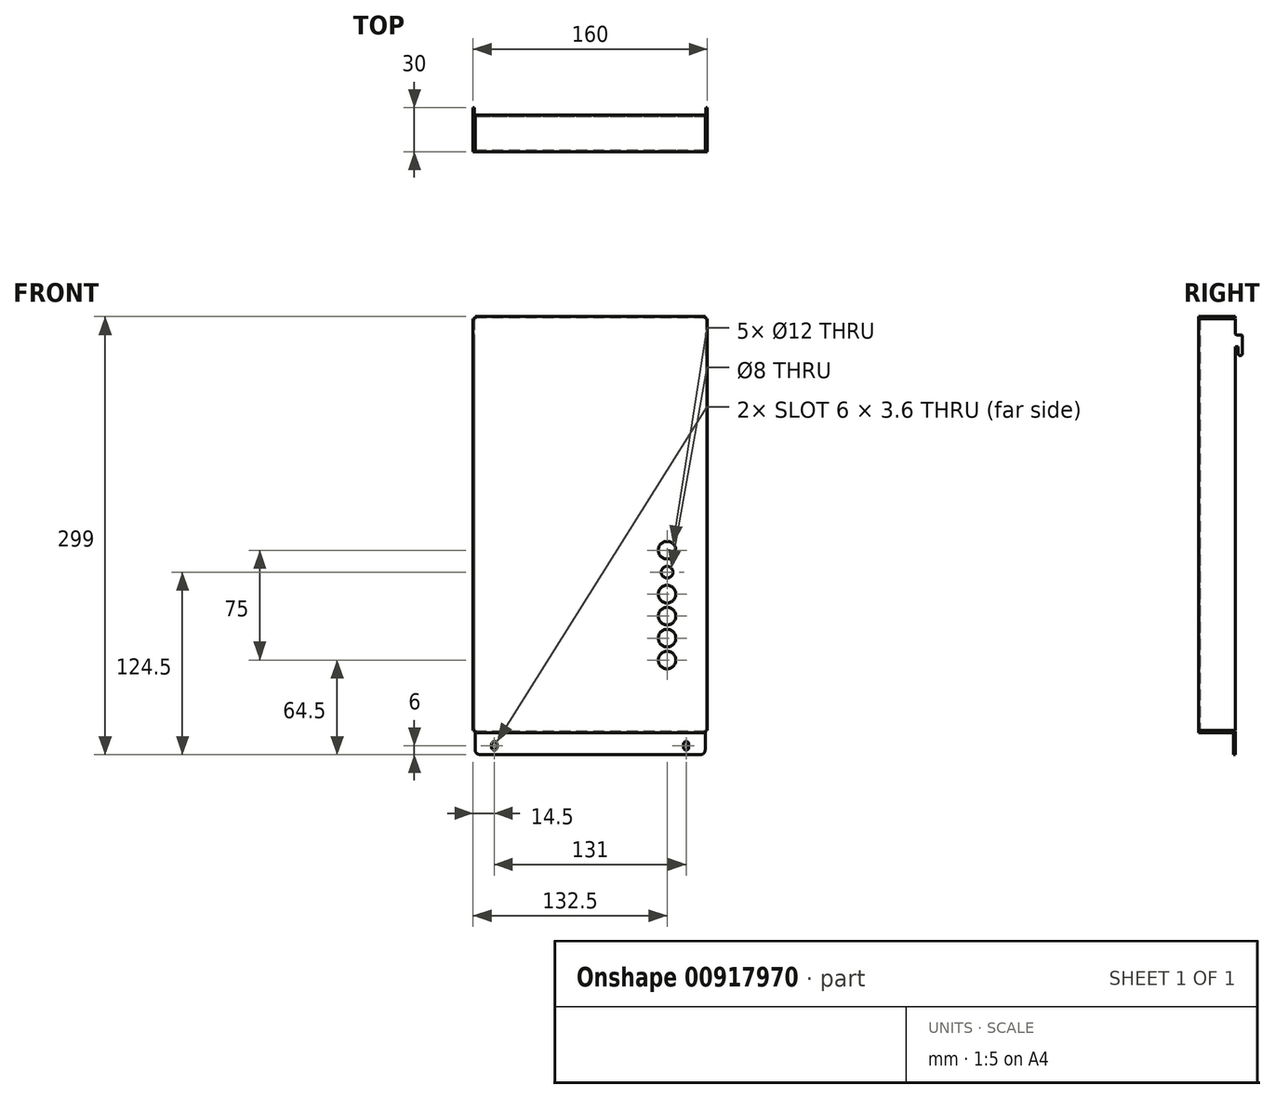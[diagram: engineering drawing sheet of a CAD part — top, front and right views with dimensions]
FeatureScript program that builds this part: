
annotation { "Feature Type Name" : "Feature", "Feature Type Description" : "" }
export const myFeature = defineFeature(function(context is Context, id is Id, definition is map)
    precondition{}
    {
        {
            var Q0;
            Q0=qCreatedBy(makeId("Front.planeOp"),FACE);
            var sketch = newSketch(context, id + "F0", { "sketchPlane" : qUnion([Q0])});
            skLineSegment(sketch, "E0.bottom", {"start": v(0, 0) * mm, "end": v(160, 0) * mm});
            skLineSegment(sketch, "E0.top", {"start": v(0, 284) * mm, "end": v(160, 284) * mm});
            skLineSegment(sketch, "E0.left", {"start": v(0, 0) * mm, "end": v(0, 284) * mm});
            skLineSegment(sketch, "E0.right", {"start": v(160, 0) * mm, "end": v(160, 284) * mm});
            skSolve(sketch);
        }
        {
            var Q0;
            Q0 = qSketchRegion(id + "F0", true);
            extrude(context, id + "F1", {"entities" : qUnion([Q0]), "depth" : 1 * mm, "offsetDistance" : 25 * mm});
        }
        {
            var Q0;
            Q0=makeQuery(id+"F1.opExtrude","CAP_FACE",FACE,{"disambiguationData":[OSD([sQuery(id+"F0.wireOp",EDGE,"E0.bottom"),sQuery(id+"F0.wireOp",EDGE,"E0.top"),sQuery(id+"F0.wireOp",EDGE,"E0.left"),sQuery(id+"F0.wireOp",EDGE,"E0.right")])],"isStart":true});
            var sketch = newSketch(context, id + "F2", { "sketchPlane" : qUnion([Q0])});
            skLineSegment(sketch, "E1.bottom", {"start": v(-160, 284) * mm, "end": v(0, 284) * mm});
            skLineSegment(sketch, "E1.top", {"start": v(-160, 0) * mm, "end": v(0, 0) * mm});
            skLineSegment(sketch, "E1.left", {"start": v(-160, 284) * mm, "end": v(-160, 0) * mm});
            skLineSegment(sketch, "E1.right", {"start": v(0, 284) * mm, "end": v(0, 0) * mm});
            skLineSegment(sketch, "E2.0", {"start": v(-1, 283) * mm, "end": v(-1, 1) * mm});
            skLineSegment(sketch, "E3.0", {"start": v(-159, 283) * mm, "end": v(-159, 1) * mm});
            skLineSegment(sketch, "E4.0", {"start": v(-159, 283) * mm, "end": v(-1, 283) * mm});
            skLineSegment(sketch, "E5.0", {"start": v(-159, 1) * mm, "end": v(-1, 1) * mm});
            skSolve(sketch);
        }
        {
            var Q0;
            Q0 = qSketchRegion(id + "F2", true);
            extrude(context, id + "F3", {"entities" : qUnion([Q0]), "operationType" : NewBodyOperationType.ADD, "depth" : 24 * mm, "offsetDistance" : 25 * mm});
        }
        {
            var Q0;
            Q0=makeQuery(id+"F1.opExtrude","CAP_FACE",FACE,{"disambiguationData":[OSD([sQuery(id+"F0.wireOp",EDGE,"E0.bottom"),sQuery(id+"F0.wireOp",EDGE,"E0.top"),sQuery(id+"F0.wireOp",EDGE,"E0.left"),sQuery(id+"F0.wireOp",EDGE,"E0.right")])],"isStart":false});
            var sketch = newSketch(context, id + "F4", { "sketchPlane" : qUnion([Q0])});
            skLineSegment(sketch, "E6.bottom", {"start": v(0, 284) * mm, "end": v(1.5, 284) * mm});
            skLineSegment(sketch, "E6.top", {"start": v(0, 282.5) * mm, "end": v(1.5, 282.5) * mm});
            skLineSegment(sketch, "E6.left", {"start": v(0, 284) * mm, "end": v(0, 282.5) * mm});
            skLineSegment(sketch, "E6.right", {"start": v(1.5, 284) * mm, "end": v(1.5, 282.5) * mm});
            skLineSegment(sketch, "E7.bottom", {"start": v(160, 284) * mm, "end": v(158.5, 284) * mm});
            skLineSegment(sketch, "E7.top", {"start": v(160, 282.5) * mm, "end": v(158.5, 282.5) * mm});
            skLineSegment(sketch, "E7.left", {"start": v(160, 284) * mm, "end": v(160, 282.5) * mm});
            skLineSegment(sketch, "E7.right", {"start": v(158.5, 284) * mm, "end": v(158.5, 282.5) * mm});
            skLineSegment(sketch, "E8.bottom", {"start": v(160, 0) * mm, "end": v(158.5, 0) * mm});
            skLineSegment(sketch, "E8.top", {"start": v(160, 1.5) * mm, "end": v(158.5, 1.5) * mm});
            skLineSegment(sketch, "E8.left", {"start": v(160, 0) * mm, "end": v(160, 1.5) * mm});
            skLineSegment(sketch, "E8.right", {"start": v(158.5, 0) * mm, "end": v(158.5, 1.5) * mm});
            skLineSegment(sketch, "E9.bottom", {"start": v(0, 0) * mm, "end": v(1.5, 0) * mm});
            skLineSegment(sketch, "E9.top", {"start": v(0, 1.5) * mm, "end": v(1.5, 1.5) * mm});
            skLineSegment(sketch, "E9.left", {"start": v(0, 0) * mm, "end": v(0, 1.5) * mm});
            skLineSegment(sketch, "E9.right", {"start": v(1.5, 0) * mm, "end": v(1.5, 1.5) * mm});
            skSolve(sketch);
        }
        {
            var Q0;
            Q0 = qSketchRegion(id + "F4", true);
            extrude(context, id + "F5", {"entities" : qUnion([Q0]), "operationType" : NewBodyOperationType.REMOVE, "endBound" : BoundingType.THROUGH_ALL, "oppositeDirection" : true, "depth" : 25 * mm, "offsetDistance" : 25 * mm});
        }
        {
            var Q0;
            Q0=makeQuery(id+"F1.opExtrude","CAP_FACE",FACE,{"disambiguationData":[OSD([sQuery(id+"F0.wireOp",EDGE,"E0.bottom"),sQuery(id+"F0.wireOp",EDGE,"E0.top"),sQuery(id+"F0.wireOp",EDGE,"E0.left"),sQuery(id+"F0.wireOp",EDGE,"E0.right")])],"isStart":false});
            var sketch = newSketch(context, id + "F6", { "sketchPlane" : qUnion([Q0])});
            skCircle(sketch, "E10", {"center": v(132.5, 124.5) * mm, "radius": 6 * mm});
            skCircle(sketch, "E11", {"center": v(132.5, 109.5) * mm, "radius": 4 * mm});
            skCircle(sketch, "E12", {"center": v(132.5, 94.5) * mm, "radius": 6 * mm});
            skCircle(sketch, "E13", {"center": v(132.5, 79.5) * mm, "radius": 6 * mm});
            skCircle(sketch, "E14", {"center": v(132.5, 64.5) * mm, "radius": 6 * mm});
            skCircle(sketch, "E15", {"center": v(132.5, 49.5) * mm, "radius": 6 * mm});
            skSolve(sketch);
        }
        {
            var Q0;
            Q0 = qSketchRegion(id + "F6", true);
            extrude(context, id + "F7", {"entities" : qUnion([Q0]), "operationType" : NewBodyOperationType.REMOVE, "endBound" : BoundingType.THROUGH_ALL, "oppositeDirection" : true, "depth" : 25 * mm, "offsetDistance" : 25 * mm});
        }
        {
            var Q0;
            Q0=makeQuery(id+"F3.boolean.opBoolean","MERGE",FACE,{"derivedFrom":[makeQuery(id+"F1.opExtrude","SWEPT_FACE",FACE,{"disambiguationData":[OSD([sQuery(id+"F0.wireOp",EDGE,"E0.bottom")])]}),makeQuery(id+"F3.opExtrude","SWEPT_FACE",FACE,{"disambiguationData":[OSD([sQuery(id+"F2.wireOp",EDGE,"E1.top")])]})]});
            var sketch = newSketch(context, id + "F8", { "sketchPlane" : qUnion([Q0])});
            skLineSegment(sketch, "E16.bottom", {"start": v(1.5, -24) * mm, "end": v(158.5, -24) * mm});
            skLineSegment(sketch, "E16.top", {"start": v(1.5, -23) * mm, "end": v(158.5, -23) * mm});
            skLineSegment(sketch, "E16.left", {"start": v(1.5, -24) * mm, "end": v(1.5, -23) * mm});
            skLineSegment(sketch, "E16.right", {"start": v(158.5, -24) * mm, "end": v(158.5, -23) * mm});
            skSolve(sketch);
        }
        {
            var Q0;
            Q0 = qSketchRegion(id + "F8", true);
            extrude(context, id + "F9", {"entities" : qUnion([Q0]), "operationType" : NewBodyOperationType.ADD, "depth" : 15 * mm, "offsetDistance" : 25 * mm});
        }
        {
            var Q0;
            Q0=makeQuery(id+"F9.opExtrude","CAP_EDGE",EDGE,{"disambiguationData":[OSD([sQuery(id+"F8.wireOp",EDGE,"E16.left")])],"isStart":false});
            var Q1;
            Q1=makeQuery(id+"F9.opExtrude","CAP_EDGE",EDGE,{"disambiguationData":[OSD([sQuery(id+"F8.wireOp",EDGE,"E16.right")])],"isStart":false});
            fillet(context, id + "F10", {"entities" : qUnion([Q0, Q1]), "radius" : 3 * mm, "tangentPropagation" : true, "allowEdgeOverflow" : false});
        }
        {
            var Q0;
            Q0=makeQuery(id+"F9.opExtrude","SWEPT_FACE",FACE,{"disambiguationData":[OSD([sQuery(id+"F8.wireOp",EDGE,"E16.top")])]});
            var sketch = newSketch(context, id + "F11", { "sketchPlane" : qUnion([Q0])});
            skLineSegment(sketch, "E17.left", {"start": v(12.7, -7.8) * mm, "end": v(12.7, -10.2) * mm});
            skLineSegment(sketch, "E17.right", {"start": v(16.3, -7.8) * mm, "end": v(16.3, -10.2) * mm});
            skLineSegment(sketch, "E18.left", {"start": v(143.7, -7.8) * mm, "end": v(143.7, -10.2) * mm});
            skLineSegment(sketch, "E18.right", {"start": v(147.3, -7.8) * mm, "end": v(147.3, -10.2) * mm});
            skArc(sketch, "E19", {"start": v(12.7, -10.2) * mm, "mid": v(14.5, -12) * mm, "end": v(16.3, -10.2) * mm});
            skArc(sketch, "E20", {"start": v(16.3, -7.8) * mm, "mid": v(14.5, -6) * mm, "end": v(12.7, -7.8) * mm});
            skArc(sketch, "E21", {"start": v(147.3, -7.8) * mm, "mid": v(145.5, -6) * mm, "end": v(143.7, -7.8) * mm});
            skArc(sketch, "E22", {"start": v(143.7, -10.2) * mm, "mid": v(145.5, -12) * mm, "end": v(147.3, -10.2) * mm});
            skPoint(sketch, "E23", {"position": v(14.5, -6) * mm});
            skPoint(sketch, "E24", {"position": v(14.5, -12) * mm});
            skPoint(sketch, "E25", {"position": v(145.5, -6) * mm});
            skPoint(sketch, "E26", {"position": v(145.5, -12) * mm});
            skSolve(sketch);
        }
        {
            var Q0;
            Q0 = qSketchRegion(id + "F11", true);
            extrude(context, id + "F12", {"entities" : qUnion([Q0]), "operationType" : NewBodyOperationType.REMOVE, "endBound" : BoundingType.THROUGH_ALL, "oppositeDirection" : true, "depth" : 25 * mm, "offsetDistance" : 25 * mm});
        }
        {
            var Q0;
            {var subQ0=sQuery(id+"F2.wireOp",EDGE,"E1.left");var subQ1=sQuery(id+"F2.wireOp",EDGE,"E3.0");Q0=makeQuery(id+"F5.boolean.opBoolean","SPLIT",FACE,{"disambiguationData":[TD([makeQuery(id+"F1.opExtrude","SWEPT_FACE",FACE,{"disambiguationData":[OSD([sQuery(id+"F0.wireOp",EDGE,"E0.right")])]})])],"derivedFrom":makeQuery(id+"F3.opExtrude","CAP_FACE",FACE,{"disambiguationData":[OSD([sQuery(id+"F2.wireOp",EDGE,"E1.bottom"),sQuery(id+"F2.wireOp",EDGE,"E1.top"),subQ0,sQuery(id+"F2.wireOp",EDGE,"E1.right"),sQuery(id+"F2.wireOp",EDGE,"E2.0"),subQ1,sQuery(id+"F2.wireOp",EDGE,"E4.0"),sQuery(id+"F2.wireOp",EDGE,"E5.0")])],"isStart":false})});}
            var sketch = newSketch(context, id + "F13", { "sketchPlane" : qUnion([Q0])});
            skLineSegment(sketch, "E27.bottom", {"start": v(-160, 271.5) * mm, "end": v(-159, 271.5) * mm});
            skLineSegment(sketch, "E27.top", {"start": v(-160, 263.5) * mm, "end": v(-159, 263.5) * mm});
            skLineSegment(sketch, "E27.left", {"start": v(-160, 271.5) * mm, "end": v(-160, 263.5) * mm});
            skLineSegment(sketch, "E27.right", {"start": v(-159, 271.5) * mm, "end": v(-159, 263.5) * mm});
            skLineSegment(sketch, "E28.bottom", {"start": v(-1, 271.5) * mm, "end": v(0, 271.5) * mm});
            skLineSegment(sketch, "E28.top", {"start": v(-1, 263.5) * mm, "end": v(0, 263.5) * mm});
            skLineSegment(sketch, "E28.left", {"start": v(-1, 271.5) * mm, "end": v(-1, 263.5) * mm});
            skLineSegment(sketch, "E28.right", {"start": v(0, 271.5) * mm, "end": v(0, 263.5) * mm});
            skSolve(sketch);
        }
        {
            var Q0;
            Q0 = qSketchRegion(id + "F13", true);
            extrude(context, id + "F14", {"entities" : qUnion([Q0]), "operationType" : NewBodyOperationType.ADD, "depth" : 5 * mm, "offsetDistance" : 25 * mm});
        }
        {
            var Q0;
            Q0=makeQuery(id+"F14.opExtrude","SWEPT_FACE",FACE,{"disambiguationData":[OSD([sQuery(id+"F13.wireOp",EDGE,"E27.top")])]});
            var sketch = newSketch(context, id + "F15", { "sketchPlane" : qUnion([Q0])});
            skLineSegment(sketch, "E29.bottom", {"start": v(160, -29) * mm, "end": v(159, -29) * mm});
            skLineSegment(sketch, "E29.top", {"start": v(160, -26) * mm, "end": v(159, -26) * mm});
            skLineSegment(sketch, "E29.left", {"start": v(160, -29) * mm, "end": v(160, -26) * mm});
            skLineSegment(sketch, "E29.right", {"start": v(159, -29) * mm, "end": v(159, -26) * mm});
            skLineSegment(sketch, "E30.bottom", {"start": v(1, -29) * mm, "end": v(0, -29) * mm});
            skLineSegment(sketch, "E30.top", {"start": v(1, -26) * mm, "end": v(0, -26) * mm});
            skLineSegment(sketch, "E30.left", {"start": v(1, -29) * mm, "end": v(1, -26) * mm});
            skLineSegment(sketch, "E30.right", {"start": v(0, -29) * mm, "end": v(0, -26) * mm});
            skSolve(sketch);
        }
        {
            var Q0;
            Q0 = qSketchRegion(id + "F15", true);
            extrude(context, id + "F16", {"entities" : qUnion([Q0]), "operationType" : NewBodyOperationType.ADD, "depth" : 6 * mm, "offsetDistance" : 25 * mm});
        }
        {
            var Q0;
            Q0=makeQuery(id+"F16.opExtrude","CAP_EDGE",EDGE,{"disambiguationData":[OSD([sQuery(id+"F15.wireOp",EDGE,"E30.top")])],"isStart":true});
            var Q1;
            Q1=makeQuery(id+"F16.opExtrude","CAP_EDGE",EDGE,{"disambiguationData":[OSD([sQuery(id+"F15.wireOp",EDGE,"E30.top")])],"isStart":false});
            var Q2;
            Q2=makeQuery(id+"F16.opExtrude","CAP_EDGE",EDGE,{"disambiguationData":[OSD([sQuery(id+"F15.wireOp",EDGE,"E30.bottom")])],"isStart":false});
            var Q3;
            Q3=makeQuery(id+"F14.opExtrude","CAP_EDGE",EDGE,{"disambiguationData":[OSD([sQuery(id+"F13.wireOp",EDGE,"E28.top")])],"isStart":true});
            var Q4;
            Q4=makeQuery(id+"F14.opExtrude","CAP_EDGE",EDGE,{"disambiguationData":[OSD([sQuery(id+"F13.wireOp",EDGE,"E28.bottom")])],"isStart":true});
            var Q5;
            Q5=makeQuery(id+"F14.opExtrude","CAP_EDGE",EDGE,{"disambiguationData":[OSD([sQuery(id+"F13.wireOp",EDGE,"E28.bottom")])],"isStart":false});
            fillet(context, id + "F17", {"entities" : qUnion([Q0, Q1, Q2, Q3, Q4, Q5]), "radius" : 1 * mm, "tangentPropagation" : true, "allowEdgeOverflow" : false});
        }
        {
            var Q0;
            Q0=makeQuery(id+"F14.opExtrude","CAP_EDGE",EDGE,{"disambiguationData":[OSD([sQuery(id+"F13.wireOp",EDGE,"E27.bottom")])],"isStart":true});
            var Q1;
            Q1=makeQuery(id+"F14.opExtrude","CAP_EDGE",EDGE,{"disambiguationData":[OSD([sQuery(id+"F13.wireOp",EDGE,"E27.bottom")])],"isStart":false});
            var Q2;
            Q2=makeQuery(id+"F16.opExtrude","CAP_EDGE",EDGE,{"disambiguationData":[OSD([sQuery(id+"F15.wireOp",EDGE,"E29.bottom")])],"isStart":false});
            var Q3;
            Q3=makeQuery(id+"F14.opExtrude","CAP_EDGE",EDGE,{"disambiguationData":[OSD([sQuery(id+"F13.wireOp",EDGE,"E27.top")])],"isStart":true});
            var Q4;
            Q4=makeQuery(id+"F16.opExtrude","CAP_EDGE",EDGE,{"disambiguationData":[OSD([sQuery(id+"F15.wireOp",EDGE,"E29.top")])],"isStart":false});
            var Q5;
            Q5=makeQuery(id+"F16.opExtrude","CAP_EDGE",EDGE,{"disambiguationData":[OSD([sQuery(id+"F15.wireOp",EDGE,"E29.top")])],"isStart":true});
            fillet(context, id + "F18", {"entities" : qUnion([Q0, Q1, Q2, Q3, Q4, Q5]), "radius" : 1 * mm, "tangentPropagation" : true, "allowEdgeOverflow" : false});
        }
    });
